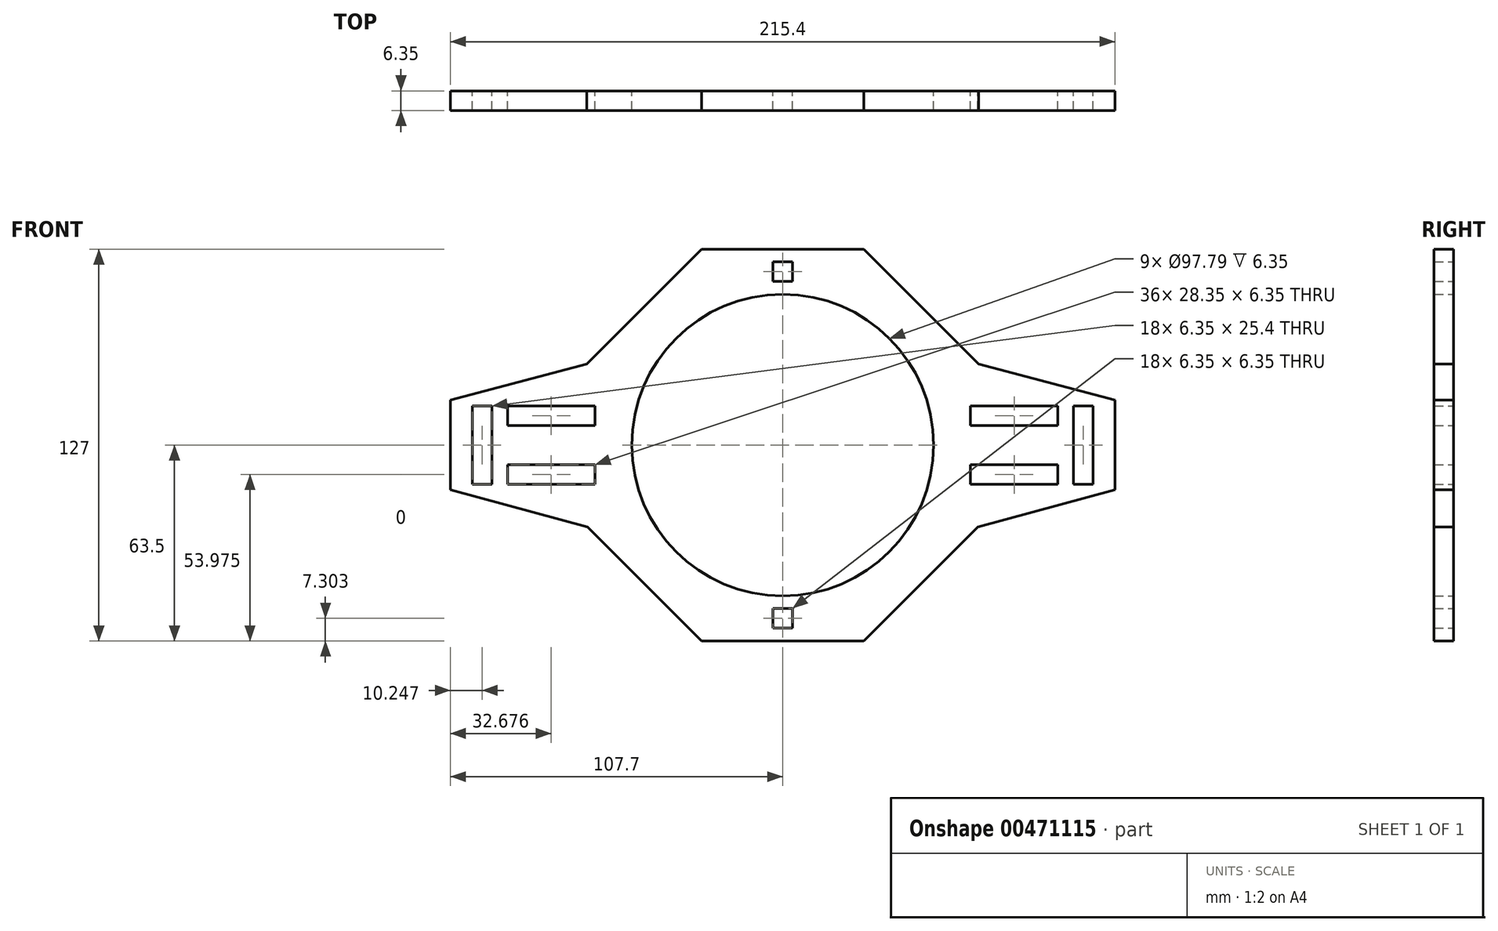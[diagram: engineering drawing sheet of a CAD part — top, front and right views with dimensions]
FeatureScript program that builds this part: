
annotation { "Feature Type Name" : "Feature", "Feature Type Description" : "" }
export const myFeature = defineFeature(function(context is Context, id is Id, definition is map)
    precondition{}
    {
        {
            var Q0;
            Q0=qCreatedBy(makeId("Front.planeOp"),FACE);
            var sketch = newSketch(context, id + "F0", { "sketchPlane" : qUnion([Q0])});
            skCircle(sketch, "E0", {"center": v(0, 0) * mm, "radius": 48.9 * mm});
            skCircle(sketch, "E1.cCircle", {"center": v(0, 0) * mm, "radius": 63.5 * mm, "construction": true});
            skLineSegment(sketch, "E1.0", {"start": v(-26.3, 63.5) * mm, "end": v(26.3, 63.5) * mm});
            skLineSegment(sketch, "E1.1", {"start": v(26.3, 63.5) * mm, "end": v(63.5, 26.3) * mm});
            skLineSegment(sketch, "E1.3", {"start": v(63.5, -26.3) * mm, "end": v(26.3, -63.5) * mm});
            skLineSegment(sketch, "E1.4", {"start": v(26.3, -63.5) * mm, "end": v(-26.3, -63.5) * mm});
            skLineSegment(sketch, "E1.5", {"start": v(-26.3, -63.5) * mm, "end": v(-63.28, -26.52) * mm});
            skLineSegment(sketch, "E1.7", {"start": v(-63.5, 26.3) * mm, "end": v(-26.3, 63.5) * mm});
            skPoint(sketch, "E1.0.midPoint", {"position": v(0, 63.5) * mm});
            skLineSegment(sketch, "E2", {"start": v(-63.5, 26.3) * mm, "end": v(-107.7, 14.57) * mm});
            skLineSegment(sketch, "E3.MirrorCS", {"start": v(-63.28, -26.52) * mm, "end": v(-107.7, -14.53) * mm});
            skCircle(sketch, "E4", {"center": v(0, 0) * mm, "radius": 47.63 * mm, "construction": true});
            skLineSegment(sketch, "E5", {"start": v(-100.63, 12.7) * mm, "end": v(-100.63, -12.7) * mm});
            skLineSegment(sketch, "E6", {"start": v(-107.7, 14.57) * mm, "end": v(-107.7, -14.53) * mm});
            skLineSegment(sketch, "E7", {"start": v(-100.63, 12.7) * mm, "end": v(-94.28, 12.7) * mm});
            skLineSegment(sketch, "E8", {"start": v(-100.63, -12.7) * mm, "end": v(-94.28, -12.7) * mm});
            skLineSegment(sketch, "E9", {"start": v(-94.28, -12.7) * mm, "end": v(-94.28, 12.7) * mm});
            skLineSegment(sketch, "E10", {"start": v(-89.2, 12.7) * mm, "end": v(-60.85, 12.7) * mm});
            skLineSegment(sketch, "E11", {"start": v(-89.2, 12.7) * mm, "end": v(-89.2, 6.35) * mm});
            skLineSegment(sketch, "E12", {"start": v(-60.85, 12.7) * mm, "end": v(-60.85, 6.35) * mm});
            skLineSegment(sketch, "E13", {"start": v(-60.85, 6.35) * mm, "end": v(-89.2, 6.35) * mm});
            skLineSegment(sketch, "E14.MirrorCS", {"start": v(-60.85, -6.35) * mm, "end": v(-89.2, -6.35) * mm});
            skLineSegment(sketch, "E15", {"start": v(-3.17, -53.02) * mm, "end": v(-3.17, -59.37) * mm});
            skLineSegment(sketch, "E16.MirrorCS", {"start": v(3.18, -53.02) * mm, "end": v(3.18, -59.37) * mm});
            skLineSegment(sketch, "E17", {"start": v(-3.17, -53.02) * mm, "end": v(3.18, -53.02) * mm});
            skLineSegment(sketch, "E18", {"start": v(3.18, -59.37) * mm, "end": v(-3.17, -59.37) * mm});
            skLineSegment(sketch, "E19.MirrorCS", {"start": v(3.18, 59.37) * mm, "end": v(-3.17, 59.37) * mm});
            skLineSegment(sketch, "E20.MirrorCS", {"start": v(-3.17, 53.02) * mm, "end": v(-3.17, 59.37) * mm});
            skLineSegment(sketch, "E21.MirrorCS", {"start": v(3.18, 53.02) * mm, "end": v(3.18, 59.37) * mm});
            skLineSegment(sketch, "E22.MirrorCS", {"start": v(-3.17, 53.02) * mm, "end": v(3.18, 53.02) * mm});
            skLineSegment(sketch, "E23", {"start": v(-89.2, -12.7) * mm, "end": v(-60.85, -12.7) * mm});
            skLineSegment(sketch, "E24", {"start": v(-60.85, -12.7) * mm, "end": v(-60.85, -6.35) * mm});
            skLineSegment(sketch, "E25", {"start": v(-89.2, -6.35) * mm, "end": v(-89.2, -12.7) * mm});
            skLineSegment(sketch, "E26", {"start": v(0, 3.32) * mm, "end": v(0, 25.33) * mm});
            skLineSegment(sketch, "E27.MirrorCS", {"start": v(89.2, 12.7) * mm, "end": v(60.85, 12.7) * mm});
            skLineSegment(sketch, "E28.MirrorCS", {"start": v(60.85, 12.7) * mm, "end": v(60.85, 6.35) * mm});
            skLineSegment(sketch, "E29.MirrorCS", {"start": v(60.85, 6.35) * mm, "end": v(89.2, 6.35) * mm});
            skLineSegment(sketch, "E30.MirrorCS", {"start": v(60.85, -6.35) * mm, "end": v(89.2, -6.35) * mm});
            skLineSegment(sketch, "E31.MirrorCS", {"start": v(60.85, -12.7) * mm, "end": v(60.85, -6.35) * mm});
            skLineSegment(sketch, "E32.MirrorCS", {"start": v(89.2, -12.7) * mm, "end": v(60.85, -12.7) * mm});
            skLineSegment(sketch, "E33.MirrorCS", {"start": v(89.2, -6.35) * mm, "end": v(89.2, -12.7) * mm});
            skLineSegment(sketch, "E34.MirrorCS", {"start": v(94.28, -12.7) * mm, "end": v(94.28, 12.7) * mm});
            skLineSegment(sketch, "E35.MirrorCS", {"start": v(100.63, 12.7) * mm, "end": v(94.28, 12.7) * mm});
            skLineSegment(sketch, "E36.MirrorCS", {"start": v(100.63, 12.7) * mm, "end": v(100.63, -12.7) * mm});
            skLineSegment(sketch, "E37.MirrorCS", {"start": v(100.63, -12.7) * mm, "end": v(94.28, -12.7) * mm});
            skLineSegment(sketch, "E38.MirrorCS", {"start": v(63.5, 26.3) * mm, "end": v(107.7, 14.57) * mm});
            skLineSegment(sketch, "E39.MirrorCS", {"start": v(107.7, 14.57) * mm, "end": v(107.7, -14.53) * mm});
            skLineSegment(sketch, "E40.MirrorCS", {"start": v(63.28, -26.52) * mm, "end": v(107.7, -14.53) * mm});
            skLineSegment(sketch, "E41.MirrorCS", {"start": v(89.2, 12.7) * mm, "end": v(89.2, 6.35) * mm});
            skSolve(sketch);
        }
        {
            var Q0;
            Q0=makeQuery(id+"F0.imprint","IMPRINT",FACE,{"disambiguationData":[TD([[makeQuery(id+"F0.imprint","IMPRINT",EDGE,{"derivedFrom":sQuery(id+"F0.wireOp",EDGE,"E0")}),-1.0]])]});
            extrude(context, id + "F1", {"entities" : qUnion([Q0]), "depth" : 6.35 * mm});
        }
    });
